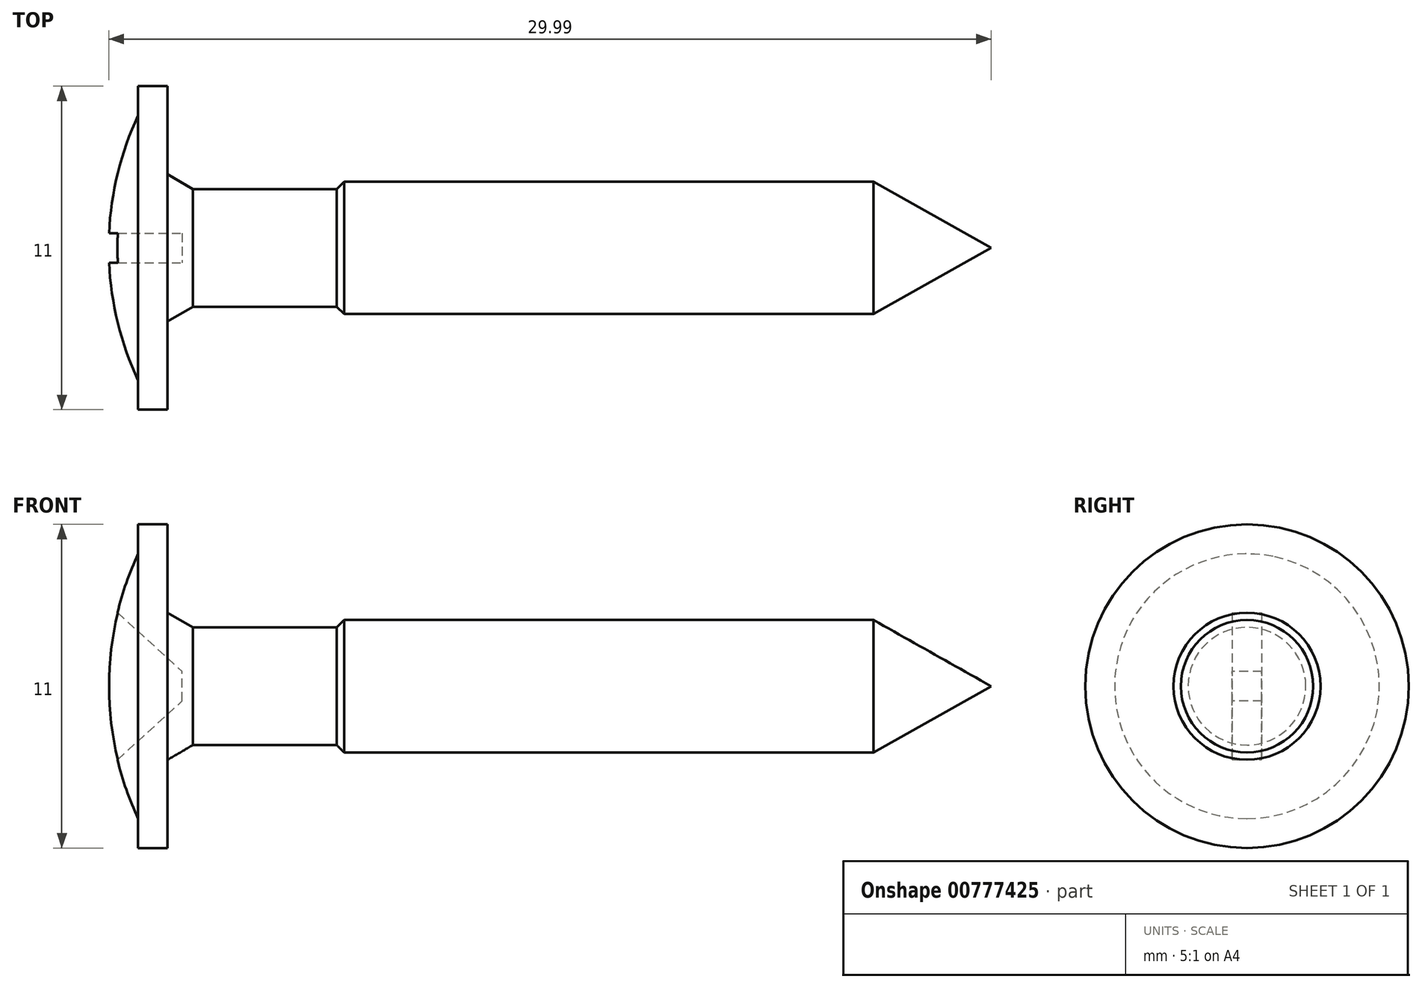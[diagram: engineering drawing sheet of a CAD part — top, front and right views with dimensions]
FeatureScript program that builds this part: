
annotation { "Feature Type Name" : "Feature", "Feature Type Description" : "" }
export const myFeature = defineFeature(function(context is Context, id is Id, definition is map)
    precondition{}
    {
        {
            var Q0;
            Q0=qCreatedBy(makeId("Front.planeOp"),FACE);
            var sketch = newSketch(context, id + "F0", { "sketchPlane" : qUnion([Q0])});
            skLineSegment(sketch, "E0", {"start": v(24, 2.25) * mm, "end": v(28, 0) * mm});
            skLineSegment(sketch, "E1", {"start": v(28, 0) * mm, "end": v(-2, 0) * mm});
            skLineSegment(sketch, "E2", {"start": v(-2, 0) * mm, "end": v(-2, 2.23) * mm, "construction": true});
            skLineSegment(sketch, "E3", {"start": v(-1, 4.5) * mm, "end": v(-1, 5.5) * mm});
            skLineSegment(sketch, "E4", {"start": v(-1, 5.5) * mm, "end": v(0, 5.5) * mm});
            skLineSegment(sketch, "E5", {"start": v(0, 5.5) * mm, "end": v(0, 2.5) * mm});
            skLineSegment(sketch, "E6", {"start": v(0, 2.5) * mm, "end": v(0.87, 2) * mm});
            skLineSegment(sketch, "E7", {"start": v(0.87, 2) * mm, "end": v(5.75, 2) * mm});
            skLineSegment(sketch, "E8", {"start": v(5.75, 2) * mm, "end": v(6, 2.25) * mm});
            skLineSegment(sketch, "E9", {"start": v(6, 2.25) * mm, "end": v(24, 2.25) * mm});
            skArc(sketch, "E10", {"start": v(-1, 4.5) * mm, "mid": v(-1.75, 2.3) * mm, "end": v(-2, 0) * mm});
            skSolve(sketch);
        }
        {
            var Q0;
            Q0 = qSketchRegion(id + "F0", true);
            var Q1;
            Q1=sQuery(id+"F0.wireOp",EDGE,"E1");
            revolve(context, id + "F1", {"surfaceOperationType" : NewSurfaceOperationType.NEW, "entities" : qUnion([Q0]), "axis" : qUnion([Q1]), "revolveType" : RevolveType.FULL});
        }
        {
            var Q0;
            Q0=qCreatedBy(makeId("Front.planeOp"),FACE);
            var sketch = newSketch(context, id + "F2", { "sketchPlane" : qUnion([Q0])});
            skLineSegment(sketch, "E11", {"start": v(-2, 2.5) * mm, "end": v(-1.7, 2.5) * mm});
            skLineSegment(sketch, "E12", {"start": v(-1.7, 2.5) * mm, "end": v(0.5, 0.5) * mm});
            skLineSegment(sketch, "E13", {"start": v(0.5, 0.5) * mm, "end": v(0.5, 0) * mm});
            skLineSegment(sketch, "E14", {"start": v(-2, 2.5) * mm, "end": v(-2, 0) * mm});
            skLineSegment(sketch, "E15.MirrorCS", {"start": v(-2, -2.5) * mm, "end": v(-2, 0) * mm});
            skLineSegment(sketch, "E16.MirrorCS", {"start": v(-2, -2.5) * mm, "end": v(-1.7, -2.5) * mm});
            skLineSegment(sketch, "E17.MirrorCS", {"start": v(-1.7, -2.5) * mm, "end": v(0.5, -0.5) * mm});
            skLineSegment(sketch, "E18.MirrorCS", {"start": v(0.5, -0.5) * mm, "end": v(0.5, 0) * mm});
            skSolve(sketch);
        }
        {
            var Q0;
            Q0 = qSketchRegion(id + "F2", true);
            extrude(context, id + "F3", {"entities" : qUnion([Q0]), "operationType" : NewBodyOperationType.REMOVE, "endBound" : BoundingType.SYMMETRIC, "oppositeDirection" : true, "depth" : 1 * mm, "offsetDistance" : 25 * mm});
        }
    });
